# Revit family: Specialty Equipment_Soap Dispenser_Metlam_ML 603 BS
name_source: partatom
category: Specialty Equipment
revit_build: Autodesk Revit 2014 (Build: 20130308_1515(x64)
units: mm (PartAtom-declared; Revit-internal decimal feet)

## types (1)
- 179w x 157h x 87d
    Assembly Code = C1030200
    Body Material = z_Metlam_Stainless Steel
    Description = Square Soap Dispenser - Button Pump Valve
    Manufacturer = Metlam
    Manufacturer_Overall Depth = 87 mm  [stored 0.285433 ft]
    Manufacturer_Overall Height = 157 mm  [stored 0.515092 ft]
    Manufacturer_Overall Width = 179 mm  [stored 0.58727 ft]
    Manufacturer_Spec Code = ML 603 BS
    Manufacturer_URL_Home Page = http://www.metlam.com.au
    Manufacturer_URL__Product Specific = http://metlam.com.au
    Model = ML 603 BS
    ModifiedIssue_ANZRS = 20151029 $
    Nozzle Material = z_Metlam_Black ABS
    Switch Material = z_Metlam_Stainless Steel
    Type Comments = Soap Dispensers
    URL = http://www.metlam.com.au

note: [stored X ft] marks values corroborated as IEEE doubles in the binary element streams (Revit-internal decimal feet)

## geometry (parser evidence)
native form markers: Sweep x2
no freeform markers — native parametric forms only
